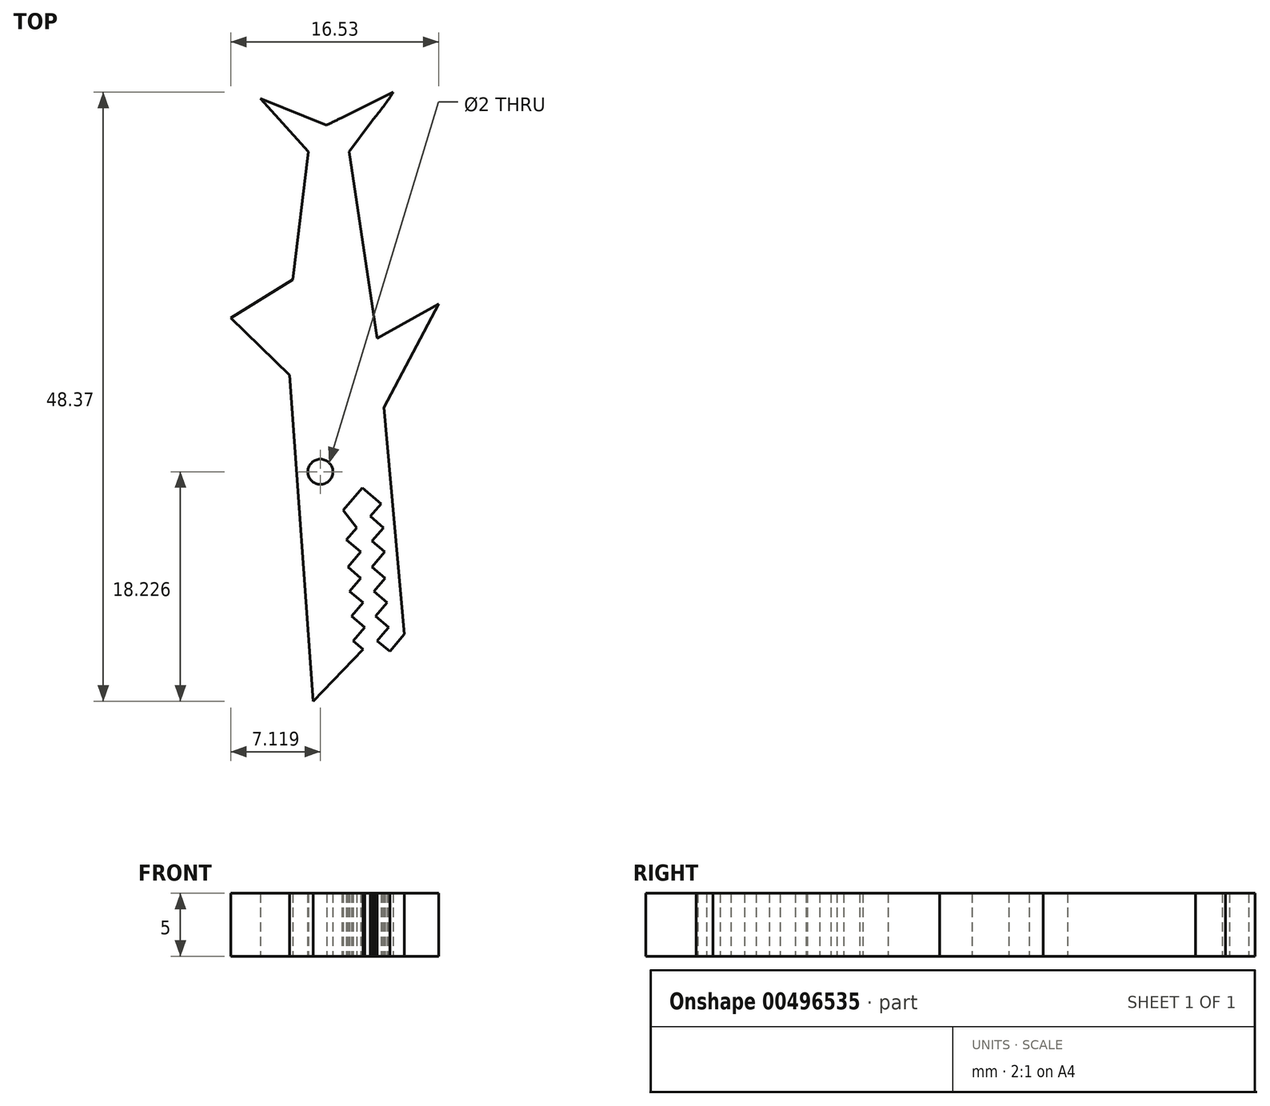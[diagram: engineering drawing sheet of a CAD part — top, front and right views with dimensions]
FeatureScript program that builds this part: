
annotation { "Feature Type Name" : "Feature", "Feature Type Description" : "" }
export const myFeature = defineFeature(function(context is Context, id is Id, definition is map)
    precondition{}
    {
        {
            var Q0;
            Q0=qCreatedBy(makeId("Top.planeOp"),FACE);
            var sketch = newSketch(context, id + "F0", { "sketchPlane" : qUnion([Q0])});
            skFitSpline(sketch, "E0", {"points": [v(7.7, 0.49) * mm, v(5.8, 26.4) * mm], "startDerivative": vector(-1.89, 25.9) * mm, "endDerivative": vector(-1.89, 25.9) * mm});
            skFitSpline(sketch, "E1", {"points": [v(5.8, 26.4) * mm, v(1.13, 30.92) * mm], "startDerivative": vector(-4.68, 4.52) * mm, "endDerivative": vector(-4.68, 4.52) * mm});
            skFitSpline(sketch, "E2", {"points": [v(1.13, 30.92) * mm, v(6.06, 33.98) * mm], "startDerivative": vector(4.93, 3.06) * mm, "endDerivative": vector(4.93, 3.06) * mm});
            skFitSpline(sketch, "E3", {"points": [v(6.06, 33.98) * mm, v(7.29, 44.14) * mm], "startDerivative": vector(1.22, 10.17) * mm, "endDerivative": vector(1.22, 10.17) * mm});
            skFitSpline(sketch, "E4", {"points": [v(7.29, 44.14) * mm, v(3.48, 48.36) * mm], "startDerivative": vector(-3.8, 4.22) * mm, "endDerivative": vector(-3.8, 4.22) * mm});
            skFitSpline(sketch, "E5", {"points": [v(3.48, 48.36) * mm, v(8.76, 46.25) * mm], "startDerivative": vector(5.28, -2.11) * mm, "endDerivative": vector(5.28, -2.11) * mm});
            skFitSpline(sketch, "E6", {"points": [v(8.76, 46.25) * mm, v(14.04, 48.86) * mm], "startDerivative": vector(3.23, 1.72) * mm, "endDerivative": vector(4.7, 2.65) * mm});
            skFitSpline(sketch, "E7", {"points": [v(14.04, 48.86) * mm, v(10.53, 44.14) * mm], "startDerivative": vector(-2.94, -4.75) * mm, "endDerivative": vector(-2.94, -4.75) * mm});
            skFitSpline(sketch, "E8", {"points": [v(10.53, 44.14) * mm, v(12.77, 29.31) * mm], "startDerivative": vector(2.24, -14.83) * mm, "endDerivative": vector(2.24, -14.83) * mm});
            skFitSpline(sketch, "E9", {"points": [v(12.77, 29.31) * mm, v(17.66, 32.04) * mm], "startDerivative": vector(4.9, 2.73) * mm, "endDerivative": vector(4.9, 2.73) * mm});
            skFitSpline(sketch, "E10", {"points": [v(17.66, 32.04) * mm, v(13.29, 23.81) * mm], "startDerivative": vector(-4.37, -8.22) * mm, "endDerivative": vector(-4.37, -8.22) * mm});
            skFitSpline(sketch, "E11", {"points": [v(13.29, 23.81) * mm, v(14.93, 5.81) * mm], "startDerivative": vector(1.64, -18) * mm, "endDerivative": vector(1.64, -18) * mm});
            skFitSpline(sketch, "E12", {"points": [v(14.93, 5.81) * mm, v(13.77, 4.47) * mm], "startDerivative": vector(-1.16, -1.35) * mm, "endDerivative": vector(-1.16, -1.35) * mm});
            skFitSpline(sketch, "E13", {"points": [v(13.77, 4.47) * mm, v(12.77, 5.29) * mm], "startDerivative": vector(-1, 0.82) * mm, "endDerivative": vector(-1, 0.82) * mm});
            skLineSegment(sketch, "E14", {"start": v(12.77, 5.29) * mm, "end": v(13.2, 5.81) * mm});
            skLineSegment(sketch, "E15", {"start": v(13.2, 5.81) * mm, "end": v(13.67, 6.37) * mm});
            skLineSegment(sketch, "E16", {"start": v(13.67, 6.37) * mm, "end": v(12.63, 7.25) * mm});
            skLineSegment(sketch, "E17", {"start": v(12.63, 7.25) * mm, "end": v(13.55, 8.33) * mm});
            skLineSegment(sketch, "E18", {"start": v(13.55, 8.33) * mm, "end": v(12.5, 9.23) * mm});
            skLineSegment(sketch, "E19", {"start": v(12.5, 9.23) * mm, "end": v(13.38, 10.28) * mm});
            skLineSegment(sketch, "E20", {"start": v(13.38, 10.28) * mm, "end": v(12.35, 11.16) * mm});
            skLineSegment(sketch, "E21", {"start": v(12.35, 11.16) * mm, "end": v(13.35, 12.34) * mm});
            skLineSegment(sketch, "E22", {"start": v(13.35, 12.34) * mm, "end": v(12.35, 13.2) * mm});
            skLineSegment(sketch, "E23", {"start": v(12.35, 13.2) * mm, "end": v(13.26, 14.27) * mm});
            skLineSegment(sketch, "E24", {"start": v(13.26, 14.27) * mm, "end": v(12.2, 15.17) * mm});
            skLineSegment(sketch, "E25", {"start": v(12.2, 15.17) * mm, "end": v(13.06, 16.18) * mm});
            skLineSegment(sketch, "E26", {"start": v(13.06, 16.18) * mm, "end": v(11.57, 17.45) * mm});
            skLineSegment(sketch, "E27", {"start": v(11.57, 17.45) * mm, "end": v(10.05, 15.67) * mm});
            skLineSegment(sketch, "E28", {"start": v(10.05, 15.67) * mm, "end": v(11.15, 14.27) * mm});
            skLineSegment(sketch, "E29", {"start": v(11.15, 14.27) * mm, "end": v(10.32, 13.3) * mm});
            skLineSegment(sketch, "E30", {"start": v(10.32, 13.3) * mm, "end": v(11.44, 12.34) * mm});
            skLineSegment(sketch, "E31", {"start": v(11.44, 12.34) * mm, "end": v(10.44, 11.16) * mm});
            skLineSegment(sketch, "E32", {"start": v(10.44, 11.16) * mm, "end": v(11.47, 10.28) * mm});
            skLineSegment(sketch, "E33", {"start": v(11.47, 10.28) * mm, "end": v(10.58, 9.23) * mm});
            skLineSegment(sketch, "E34", {"start": v(10.58, 9.23) * mm, "end": v(11.64, 8.33) * mm});
            skLineSegment(sketch, "E35", {"start": v(11.64, 8.33) * mm, "end": v(10.72, 7.25) * mm});
            skLineSegment(sketch, "E36", {"start": v(10.72, 7.25) * mm, "end": v(11.76, 6.37) * mm});
            skLineSegment(sketch, "E37", {"start": v(11.76, 6.37) * mm, "end": v(10.84, 5.29) * mm});
            skLineSegment(sketch, "E38", {"start": v(10.84, 5.29) * mm, "end": v(11.64, 4.6) * mm});
            skLineSegment(sketch, "E39", {"start": v(11.64, 4.6) * mm, "end": v(7.7, 0.49) * mm});
            skLineSegment(sketch, "E40", {"start": v(7.7, 0.49) * mm, "end": v(5.8, 26.4) * mm});
            skLineSegment(sketch, "E41", {"start": v(5.8, 26.4) * mm, "end": v(1.13, 30.92) * mm});
            skLineSegment(sketch, "E42", {"start": v(1.13, 30.92) * mm, "end": v(6.06, 33.98) * mm});
            skLineSegment(sketch, "E43", {"start": v(6.06, 33.98) * mm, "end": v(7.29, 44.14) * mm});
            skLineSegment(sketch, "E44", {"start": v(7.29, 44.14) * mm, "end": v(3.48, 48.36) * mm});
            skLineSegment(sketch, "E45", {"start": v(3.48, 48.36) * mm, "end": v(8.76, 46.25) * mm});
            skLineSegment(sketch, "E46", {"start": v(8.76, 46.25) * mm, "end": v(14.04, 48.86) * mm});
            skLineSegment(sketch, "E47", {"start": v(14.04, 48.86) * mm, "end": v(10.53, 44.14) * mm});
            skLineSegment(sketch, "E48", {"start": v(10.53, 44.14) * mm, "end": v(12.77, 29.31) * mm});
            skLineSegment(sketch, "E49", {"start": v(12.77, 29.31) * mm, "end": v(17.66, 32.04) * mm});
            skLineSegment(sketch, "E50", {"start": v(17.66, 32.04) * mm, "end": v(13.29, 23.81) * mm});
            skLineSegment(sketch, "E51", {"start": v(13.29, 23.81) * mm, "end": v(14.93, 5.81) * mm});
            skLineSegment(sketch, "E52", {"start": v(14.93, 5.81) * mm, "end": v(13.77, 4.47) * mm});
            skLineSegment(sketch, "E53", {"start": v(13.77, 4.47) * mm, "end": v(12.77, 5.29) * mm});
            skCircle(sketch, "E54", {"center": v(8.25, 18.72) * mm, "radius": 1 * mm});
            skSolve(sketch);
        }
        {
            var Q0;
            Q0 = qSketchRegion(id + "F0", true);
            extrude(context, id + "F1", {"entities" : qUnion([Q0]), "depth" : 5 * mm, "offsetDistance" : 25 * mm});
        }
    });
